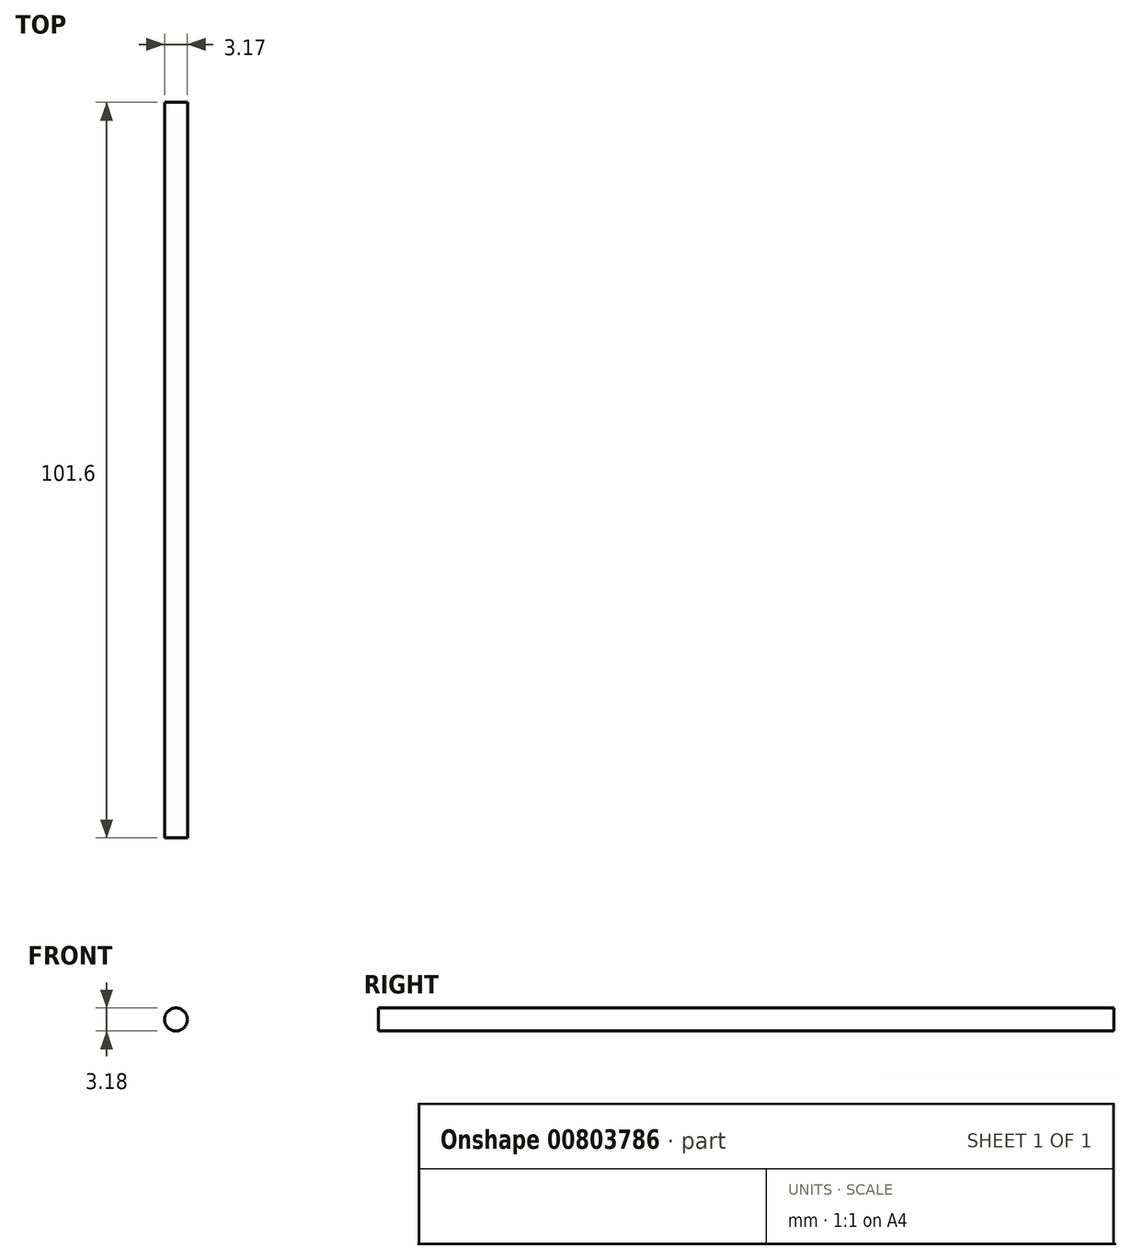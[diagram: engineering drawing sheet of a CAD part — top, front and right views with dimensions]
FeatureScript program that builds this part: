
annotation { "Feature Type Name" : "Feature", "Feature Type Description" : "" }
export const myFeature = defineFeature(function(context is Context, id is Id, definition is map)
    precondition{}
    {
        {
            var Q0;
            Q0=qCreatedBy(makeId("Front.planeOp"),FACE);
            var sketch = newSketch(context, id + "F0", { "sketchPlane" : qUnion([Q0])});
            skCircle(sketch, "E0", {"center": v(-35.62, 20.59) * mm, "radius": 1.59 * mm});
            skSolve(sketch);
        }
        {
            var Q0;
            Q0=makeQuery(id+"F0.imprint","IMPRINT",FACE,{"disambiguationData":[TD([[makeQuery(id+"F0.imprint","IMPRINT",EDGE,{"derivedFrom":sQuery(id+"F0.wireOp",EDGE,"E0")}),1.0]])]});
            extrude(context, id + "F1", {"entities" : qUnion([Q0]), "depth" : 101.6 * mm, "offsetDistance" : 25.4 * mm});
        }
    });
